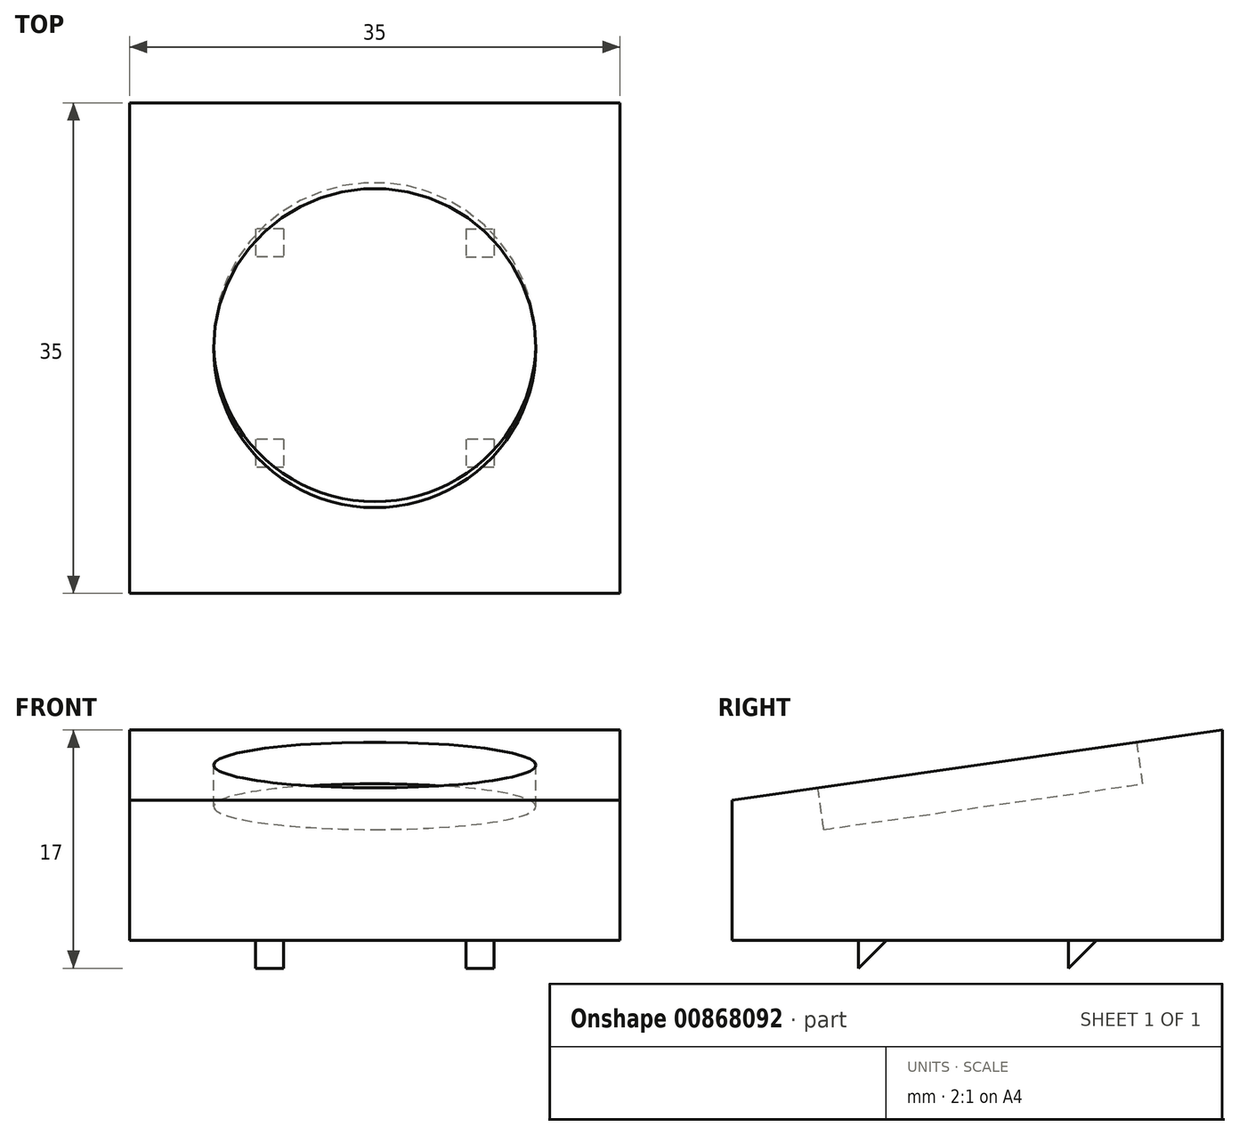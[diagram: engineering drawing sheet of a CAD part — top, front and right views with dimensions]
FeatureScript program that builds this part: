
annotation { "Feature Type Name" : "Feature", "Feature Type Description" : "" }
export const myFeature = defineFeature(function(context is Context, id is Id, definition is map)
    precondition{}
    {
        {
            var Q0;
            Q0=qCreatedBy(makeId("Top.planeOp"),FACE);
            var sketch = newSketch(context, id + "F0", { "sketchPlane" : qUnion([Q0])});
            skLineSegment(sketch, "E0.bottom", {"start": v(17.5, 17.5) * mm, "end": v(-17.5, 17.5) * mm});
            skLineSegment(sketch, "E0.top", {"start": v(17.5, -17.5) * mm, "end": v(-17.5, -17.5) * mm});
            skLineSegment(sketch, "E0.left", {"start": v(17.5, 17.5) * mm, "end": v(17.5, -17.5) * mm});
            skLineSegment(sketch, "E0.right", {"start": v(-17.5, 17.5) * mm, "end": v(-17.5, -17.5) * mm});
            skPoint(sketch, "E0.middle", {"position": v(0, 0) * mm});
            skLineSegment(sketch, "E1", {"start": v(-7.5, 17.5) * mm, "end": v(-7.5, -17.5) * mm, "construction": true});
            skLineSegment(sketch, "E2", {"start": v(7.5, 17.5) * mm, "end": v(7.5, -17.5) * mm, "construction": true});
            skLineSegment(sketch, "E3", {"start": v(-17.5, 17.5) * mm, "end": v(17.5, -17.5) * mm, "construction": true});
            skLineSegment(sketch, "E4", {"start": v(17.5, 17.5) * mm, "end": v(-17.5, -17.5) * mm, "construction": true});
            skLineSegment(sketch, "E5.bottom", {"start": v(-6.5, 8.5) * mm, "end": v(-8.5, 8.5) * mm});
            skLineSegment(sketch, "E5.top", {"start": v(-6.5, 6.5) * mm, "end": v(-8.5, 6.5) * mm});
            skLineSegment(sketch, "E5.left", {"start": v(-6.5, 8.5) * mm, "end": v(-6.5, 6.5) * mm});
            skLineSegment(sketch, "E5.right", {"start": v(-8.5, 8.5) * mm, "end": v(-8.5, 6.5) * mm});
            skPoint(sketch, "E5.middle", {"position": v(-7.5, 7.5) * mm});
            skLineSegment(sketch, "E6.bottom", {"start": v(6.5, 8.5) * mm, "end": v(8.5, 8.5) * mm});
            skLineSegment(sketch, "E6.top", {"start": v(6.5, 6.5) * mm, "end": v(8.5, 6.5) * mm});
            skLineSegment(sketch, "E6.left", {"start": v(6.5, 8.5) * mm, "end": v(6.5, 6.5) * mm});
            skLineSegment(sketch, "E6.right", {"start": v(8.5, 8.5) * mm, "end": v(8.5, 6.5) * mm});
            skPoint(sketch, "E6.middle", {"position": v(7.5, 7.5) * mm});
            skLineSegment(sketch, "E7.bottom", {"start": v(8.5, -6.5) * mm, "end": v(6.5, -6.5) * mm});
            skLineSegment(sketch, "E7.top", {"start": v(8.5, -8.5) * mm, "end": v(6.5, -8.5) * mm});
            skLineSegment(sketch, "E7.left", {"start": v(8.5, -6.5) * mm, "end": v(8.5, -8.5) * mm});
            skLineSegment(sketch, "E7.right", {"start": v(6.5, -6.5) * mm, "end": v(6.5, -8.5) * mm});
            skPoint(sketch, "E7.middle", {"position": v(7.5, -7.5) * mm});
            skLineSegment(sketch, "E8.bottom", {"start": v(-6.5, -6.5) * mm, "end": v(-8.5, -6.5) * mm});
            skLineSegment(sketch, "E8.top", {"start": v(-6.5, -8.5) * mm, "end": v(-8.5, -8.5) * mm});
            skLineSegment(sketch, "E8.left", {"start": v(-6.5, -6.5) * mm, "end": v(-6.5, -8.5) * mm});
            skLineSegment(sketch, "E8.right", {"start": v(-8.5, -6.5) * mm, "end": v(-8.5, -8.5) * mm});
            skPoint(sketch, "E8.middle", {"position": v(-7.5, -7.5) * mm});
            skSolve(sketch);
        }
        {
            var Q0;
            Q0=makeQuery(id+"F0.imprint","IMPRINT",FACE,{"disambiguationData":[TD([[makeQuery(id+"F0.imprint","IMPRINT",EDGE,{"derivedFrom":sQuery(id+"F0.wireOp",EDGE,"E0.bottom")}),1.0]])]});
            var Q1;
            Q1=makeQuery(id+"F0.imprint","IMPRINT",FACE,{"disambiguationData":[TD([[makeQuery(id+"F0.imprint","IMPRINT",EDGE,{"derivedFrom":sQuery(id+"F0.wireOp",EDGE,"E5.bottom")}),1.0]])]});
            var Q2;
            Q2=makeQuery(id+"F0.imprint","IMPRINT",FACE,{"disambiguationData":[TD([[makeQuery(id+"F0.imprint","IMPRINT",EDGE,{"derivedFrom":sQuery(id+"F0.wireOp",EDGE,"E6.bottom")}),-1.0]])]});
            var Q3;
            Q3=makeQuery(id+"F0.imprint","IMPRINT",FACE,{"disambiguationData":[TD([[makeQuery(id+"F0.imprint","IMPRINT",EDGE,{"derivedFrom":sQuery(id+"F0.wireOp",EDGE,"E8.bottom")}),1.0]])]});
            var Q4;
            Q4=makeQuery(id+"F0.imprint","IMPRINT",FACE,{"disambiguationData":[TD([[makeQuery(id+"F0.imprint","IMPRINT",EDGE,{"derivedFrom":sQuery(id+"F0.wireOp",EDGE,"E7.bottom")}),1.0]])]});
            extrude(context, id + "F1", {"entities" : qUnion([Q0, Q1, Q2, Q3, Q4]), "depth" : 15 * mm, "offsetDistance" : 25 * mm});
        }
        {
            var Q0;
            Q0=makeQuery(id+"F1.opExtrude","CAP_EDGE",EDGE,{"disambiguationData":[OSD([sQuery(id+"F0.wireOp",EDGE,"E0.top")])],"isStart":false});
            chamfer(context, id + "F2", {"entities" : qUnion([Q0]), "chamferType" : ChamferType.TWO_OFFSETS, "width1" : 5 * mm, "oppositeDirection" : false, "width2" : 35 * mm, "tangentPropagation" : true});
        }
        {
            var Q0;
            Q0=makeQuery(id+"F0.imprint","IMPRINT",FACE,{"disambiguationData":[TD([[makeQuery(id+"F0.imprint","IMPRINT",EDGE,{"derivedFrom":sQuery(id+"F0.wireOp",EDGE,"E8.bottom")}),1.0]])]});
            var Q1;
            Q1=makeQuery(id+"F0.imprint","IMPRINT",FACE,{"disambiguationData":[TD([[makeQuery(id+"F0.imprint","IMPRINT",EDGE,{"derivedFrom":sQuery(id+"F0.wireOp",EDGE,"E7.bottom")}),1.0]])]});
            var Q2;
            Q2=makeQuery(id+"F0.imprint","IMPRINT",FACE,{"disambiguationData":[TD([[makeQuery(id+"F0.imprint","IMPRINT",EDGE,{"derivedFrom":sQuery(id+"F0.wireOp",EDGE,"E6.bottom")}),-1.0]])]});
            var Q3;
            Q3=makeQuery(id+"F0.imprint","IMPRINT",FACE,{"disambiguationData":[TD([[makeQuery(id+"F0.imprint","IMPRINT",EDGE,{"derivedFrom":sQuery(id+"F0.wireOp",EDGE,"E5.bottom")}),1.0]])]});
            extrude(context, id + "F3", {"entities" : qUnion([Q0, Q1, Q2, Q3]), "operationType" : NewBodyOperationType.ADD, "oppositeDirection" : true, "depth" : 3 * mm, "offsetDistance" : 25 * mm});
        }
        {
            var Q0;
            Q0=makeQuery(id+"F3.opExtrude","CAP_EDGE",EDGE,{"disambiguationData":[OSD([sQuery(id+"F0.wireOp",EDGE,"E8.bottom")])],"isStart":false});
            var Q1;
            Q1=makeQuery(id+"F3.opExtrude","CAP_EDGE",EDGE,{"disambiguationData":[OSD([sQuery(id+"F0.wireOp",EDGE,"E7.bottom")])],"isStart":false});
            var Q2;
            Q2=makeQuery(id+"F3.opExtrude","CAP_EDGE",EDGE,{"disambiguationData":[OSD([sQuery(id+"F0.wireOp",EDGE,"E6.bottom")])],"isStart":false});
            var Q3;
            Q3=makeQuery(id+"F3.opExtrude","CAP_EDGE",EDGE,{"disambiguationData":[OSD([sQuery(id+"F0.wireOp",EDGE,"E5.bottom")])],"isStart":false});
            chamfer(context, id + "F4", {"entities" : qUnion([Q0, Q1, Q2, Q3]), "width" : 3 * mm, "tangentPropagation" : true});
        }
        {
            var Q0;
            Q0=makeQuery(id+"F2.opChamfer","BLEND_FACE",FACE,{"disambiguationData":[OSD([sQuery(id+"F0.wireOp",EDGE,"E0.top")])]});
            var sketch = newSketch(context, id + "F5", { "sketchPlane" : qUnion([Q0])});
            skLineSegment(sketch, "E9", {"start": v(17.5, -15.9) * mm, "end": v(-17.5, 19.45) * mm, "construction": true});
            skLineSegment(sketch, "E10", {"start": v(-17.5, -15.9) * mm, "end": v(17.5, 19.45) * mm, "construction": true});
            skPoint(sketch, "E11", {"position": v(0, 1.77) * mm});
            skCircle(sketch, "E12", {"center": v(0, 1.77) * mm, "radius": 11.5 * mm});
            skSolve(sketch);
        }
        {
            var Q0;
            Q0=makeQuery(id+"F5.imprint","IMPRINT",FACE,{"disambiguationData":[TD([[makeQuery(id+"F5.imprint","IMPRINT",EDGE,{"derivedFrom":sQuery(id+"F5.wireOp",EDGE,"E12")}),1.0]])]});
            extrude(context, id + "F6", {"entities" : qUnion([Q0]), "operationType" : NewBodyOperationType.REMOVE, "oppositeDirection" : true, "depth" : 3 * mm, "offsetDistance" : 25 * mm});
        }
    });
